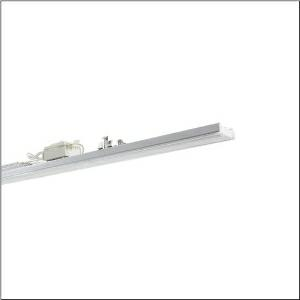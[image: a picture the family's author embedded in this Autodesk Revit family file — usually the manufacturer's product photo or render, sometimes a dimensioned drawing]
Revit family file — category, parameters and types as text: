
# Revit family: licross_r__21_recessed_mo_52tl18vn48xg_e29d
name_source: partatom
category: Lighting Fixtures
units: mm (PartAtom-declared; Revit-internal decimal feet)

## family parameters
Cut with Voids When Loaded = No
Host = Face
Light Source = No
Part Type = Normal
Room Calculation Point = No
Round Connector Dimension = Use Diameter
Shared = No

## types (1)
- --- (1 x LED, 8000 lm, 45.7 W, 4000K)
    Apparent Load = 46 VA
    CIE Flux Codes = 79 95 99 100 100
    Color Rendering = 80
    Color Temperature = 4000K
    Default Elevation = 1800 mm
    Description = Licross® 21 Recessed MO, luminaire insert, of sheet steel, galvanised, coil coated, white, length: 1.500mm, width: 66mm, height: 67mm, LED rated luminous flux: 8.000lm, light colour: 840, control gear: DALI 2, CLO, with plug, 5-pole, with phase selection, mains connection: 220..240V, AC, 50/60Hz, start of lifetime: 46W, end of service life: 54W, halogen-free wiring, primary optical cover: cover, of PMMA, light emission: direct distribution, primary light characteristic: symmetric, protection rating (complete): IP40, insulation class (complete): insulation class I (protective earthing), certification: CE, ENEC, VDE, UKCA, protection symbol: D if used in an environment without relevant dust loads with corresponding accessories, impact resistance: IK06, permissible ambient temperature for indoor applications: -25..+40°C, corresponds to IFS (International Featured Standards) requirements for safety and quality in the food industry, reducing of maximum allowable ambient temperature of 5°C with ceiling mounting, LABS conformity tested according to VDMA 24364:2018-05, packaging unit: 1 piece
    Height = 58 mm
    Lamp = 1 x LED
    Lamp Light Flux = 8000 lm
    Lamp Power = 45.7 W
    Lamp count = 1
    Length = 1500 mm
    Luminous efficacy = 175 lm/W
    Manufacturer = Siteco
    ModVariant = No
    Model = 52TL18VN48XG
    Mounting Place = Ceiling
    Mounting Type = Pendant
    Number of Poles = 1
    OnlyDefault = Yes
    Power Factor = 1
    Product Name = Licross® 21 Recessed MO
    Product group = luminaire insert
    ProductGroupID = 902
    Protection Class = Protection class I
    Protection Degree = IP 40
    RLX_Detail_Level = 1
    RLX_Emergency_Light_Flux = 0 lm
    RLX_Emergency_Type = 0
    RLX_Emergency_Type_DB = No
    RlxData = <blob elided: 24553 chars, md5=c0b0c623>
    Socket = socket
    Standby Power = 0 W
    System Light Flux = 8000 lm
    System Power = 46 W
    Type Comments = factory setting: luminous flux: 100 % | dim-lin: 254 | 307 mA
    Type Image = l_1296930.jpg
    URL = http://relux.com
    VarID = @adj_082278
    Voltage = 0 V
    Weight = 0.00 kg
    Width = 66 mm

## geometry (parser evidence)
native form markers: Blend x4, Sweep x11
no freeform markers — native parametric forms only
